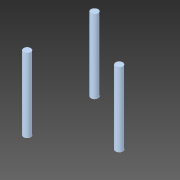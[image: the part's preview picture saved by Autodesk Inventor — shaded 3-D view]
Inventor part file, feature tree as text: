
AUTODESK INVENTOR PART (.ipt)
format: ipt  version: 2020.1 (Build 241239000, 239)  size: 86,016 bytes
history: native  units: mm
features: extrude x1, other x1
ambient origin geometry x8: Origin, YZ Plane, XZ Plane, XY Plane, X Axis, Y Axis, Z Axis, Center Point
bodies: Solid1 (feature_tree)
feature tree (2):
  extrude  "Extrude Rig Columns"  Depth=30.0mm
  other  "Locate Rig Columns"
